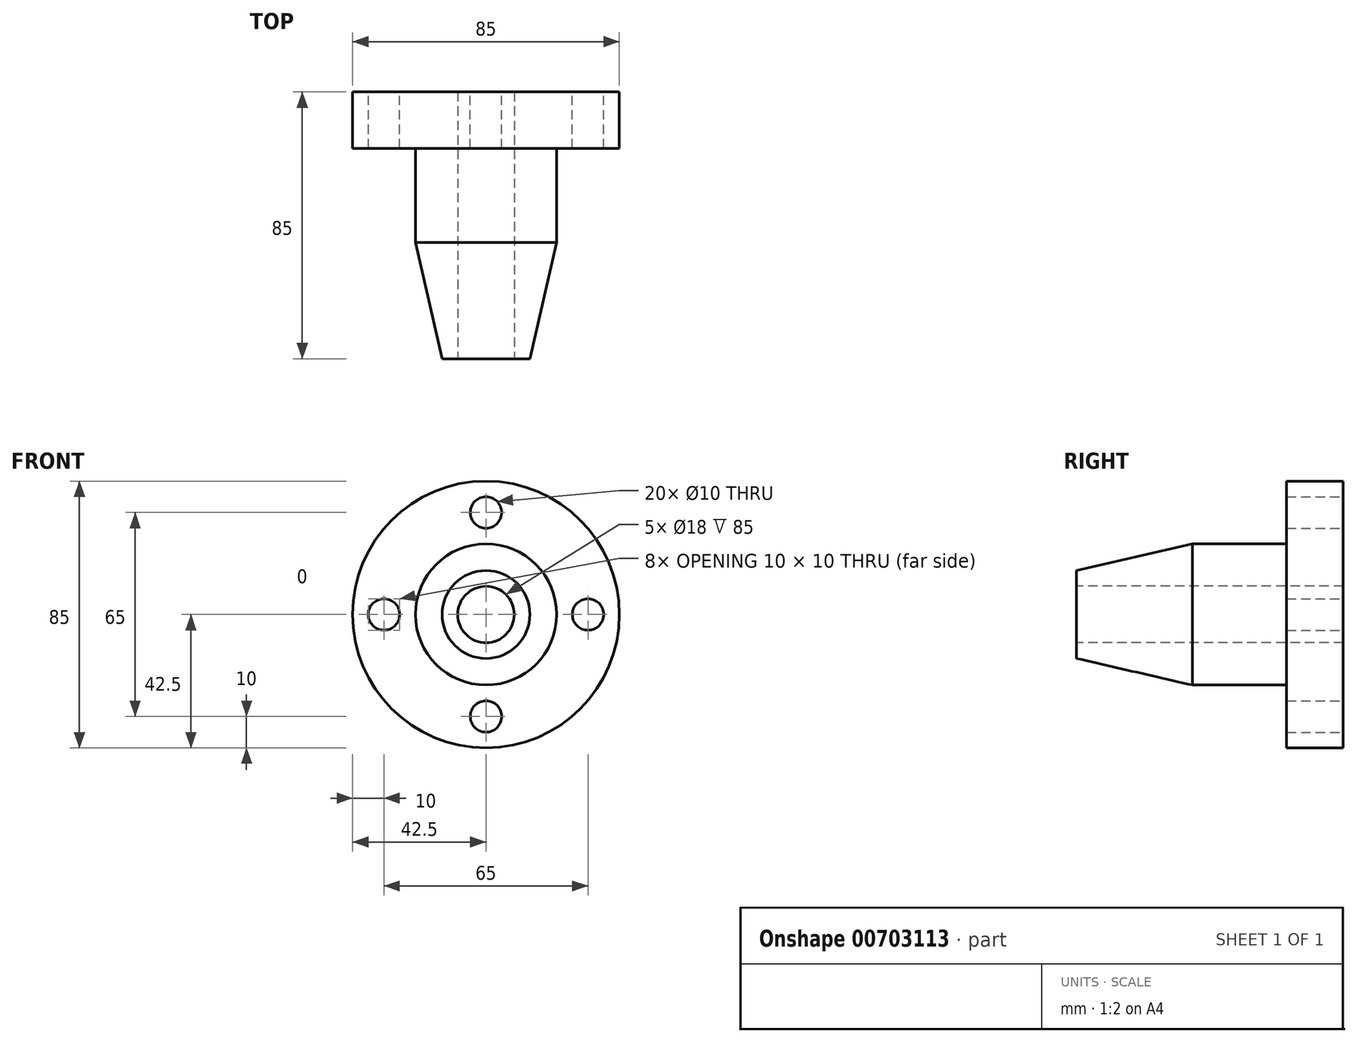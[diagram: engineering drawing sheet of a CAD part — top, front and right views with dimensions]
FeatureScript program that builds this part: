
annotation { "Feature Type Name" : "Feature", "Feature Type Description" : "" }
export const myFeature = defineFeature(function(context is Context, id is Id, definition is map)
    precondition{}
    {
        {
            var Q0;
            Q0=qCreatedBy(makeId("Top.planeOp"),FACE);
            var sketch = newSketch(context, id + "F0", { "sketchPlane" : qUnion([Q0])});
            skLineSegment(sketch, "E0", {"start": v(0, -52.11) * mm, "end": v(0, 53.56) * mm, "construction": true});
            skLineSegment(sketch, "E1", {"start": v(9, -43.15) * mm, "end": v(14, -43.15) * mm});
            skLineSegment(sketch, "E2", {"start": v(14, -43.15) * mm, "end": v(22.5, -6.15) * mm});
            skLineSegment(sketch, "E3", {"start": v(22.5, -6.15) * mm, "end": v(22.5, 23.85) * mm});
            skLineSegment(sketch, "E4", {"start": v(22.5, 23.85) * mm, "end": v(42.5, 23.85) * mm});
            skLineSegment(sketch, "E5", {"start": v(42.5, 23.85) * mm, "end": v(42.5, 41.85) * mm});
            skLineSegment(sketch, "E6", {"start": v(42.5, 41.85) * mm, "end": v(9, 41.85) * mm});
            skLineSegment(sketch, "E7", {"start": v(9, 41.85) * mm, "end": v(9, -43.15) * mm});
            skSolve(sketch);
        }
        {
            var Q0;
            Q0 = qSketchRegion(id + "F0", true);
            var Q1;
            Q1=sQuery(id+"F0.wireOp",EDGE,"E0");
            revolve(context, id + "F1", {"surfaceOperationType" : NewSurfaceOperationType.NEW, "entities" : qUnion([Q0]), "axis" : qUnion([Q1]), "revolveType" : RevolveType.FULL});
        }
        {
            var Q0;
            Q0=makeQuery(id+"F1.opRevolve","SWEPT_FACE",FACE,{"disambiguationData":[OSD([sQuery(id+"F0.wireOp",EDGE,"E6")])]});
            var sketch = newSketch(context, id + "F2", { "sketchPlane" : qUnion([Q0])});
            skCircle(sketch, "E8", {"center": v(-32.5, 0) * mm, "radius": 5 * mm});
            skCircle(sketch, "E9.1.0", {"center": v(0, -32.5) * mm, "radius": 5 * mm});
            skCircle(sketch, "E9.2.0", {"center": v(32.5, 0) * mm, "radius": 5 * mm});
            skCircle(sketch, "E9.3.0", {"center": v(0, 32.5) * mm, "radius": 5 * mm});
            skPoint(sketch, "E9.center", {"position": v(0, 0) * mm});
            skSolve(sketch);
        }
        {
            var Q0;
            Q0 = qSketchRegion(id + "F2", true);
            extrude(context, id + "F3", {"entities" : qUnion([Q0]), "operationType" : NewBodyOperationType.REMOVE, "endBound" : BoundingType.THROUGH_ALL, "oppositeDirection" : true, "depth" : 25.4 * mm, "offsetDistance" : 25.4 * mm});
        }
    });
